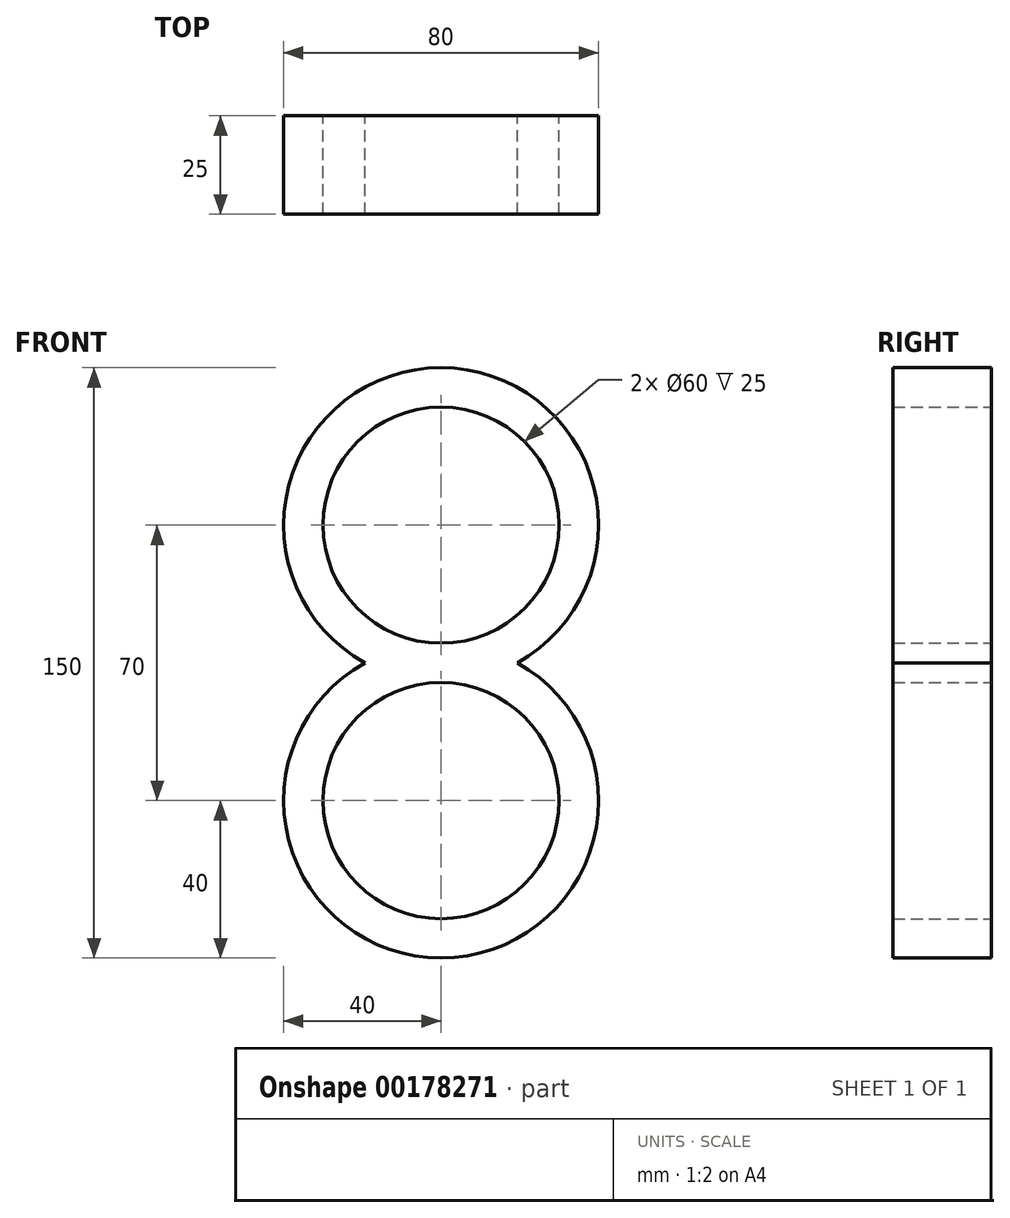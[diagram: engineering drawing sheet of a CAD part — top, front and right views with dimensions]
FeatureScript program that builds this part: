
annotation { "Feature Type Name" : "Feature", "Feature Type Description" : "" }
export const myFeature = defineFeature(function(context is Context, id is Id, definition is map)
    precondition{}
    {
        {
            var Q0;
            Q0=qCreatedBy(makeId("Front.planeOp"),FACE);
            var sketch = newSketch(context, id + "F0", { "sketchPlane" : qUnion([Q0])});
            skCircle(sketch, "E0", {"center": v(0, 0) * mm, "radius": 30 * mm});
            skCircle(sketch, "E1", {"center": v(0, 0) * mm, "radius": 40 * mm});
            skCircle(sketch, "E2", {"center": v(0, -70) * mm, "radius": 40 * mm});
            skCircle(sketch, "E3", {"center": v(0, -70) * mm, "radius": 30 * mm});
            skSolve(sketch);
        }
        {
            var Q0;
            Q0=makeQuery(id+"F0.imprint","IMPRINT",FACE,{"disambiguationData":[TD([[makeQuery(id+"F0.imprint","IMPRINT",EDGE,{"derivedFrom":sQuery(id+"F0.wireOp",EDGE,"E0")}),-1.0]])]});
            var Q1;
            {var subQ0=sQuery(id+"F0.wireOp",EDGE,"E3");Q1=makeQuery(id+"F0.imprint","IMPRINT",FACE,{"disambiguationData":[TD([[makeQuery(id+"F0.imprint","IMPRINT",EDGE,{"derivedFrom":subQ0}),-1.0]])]});}
            var Q2;
            {var subQ0=sQuery(id+"F0.wireOp",EDGE,"E1");var subQ1=makeQuery(id+"F0.imprint","INTERSECT",VERTEX,{"derivedFrom":[subQ0,sQuery(id+"F0.wireOp",EDGE,"E3")]});Q2=makeQuery(id+"F0.imprint","IMPRINT",FACE,{"disambiguationData":[TD([[makeQuery(id+"F0.imprint","IMPRINT",EDGE,{"disambiguationData":[TD([[subQ1,1.0]])],"derivedFrom":subQ0}),1.0]])]});}
            extrude(context, id + "F1", {"entities" : qUnion([Q0, Q1, Q2]), "depth" : 25 * mm});
        }
    });
